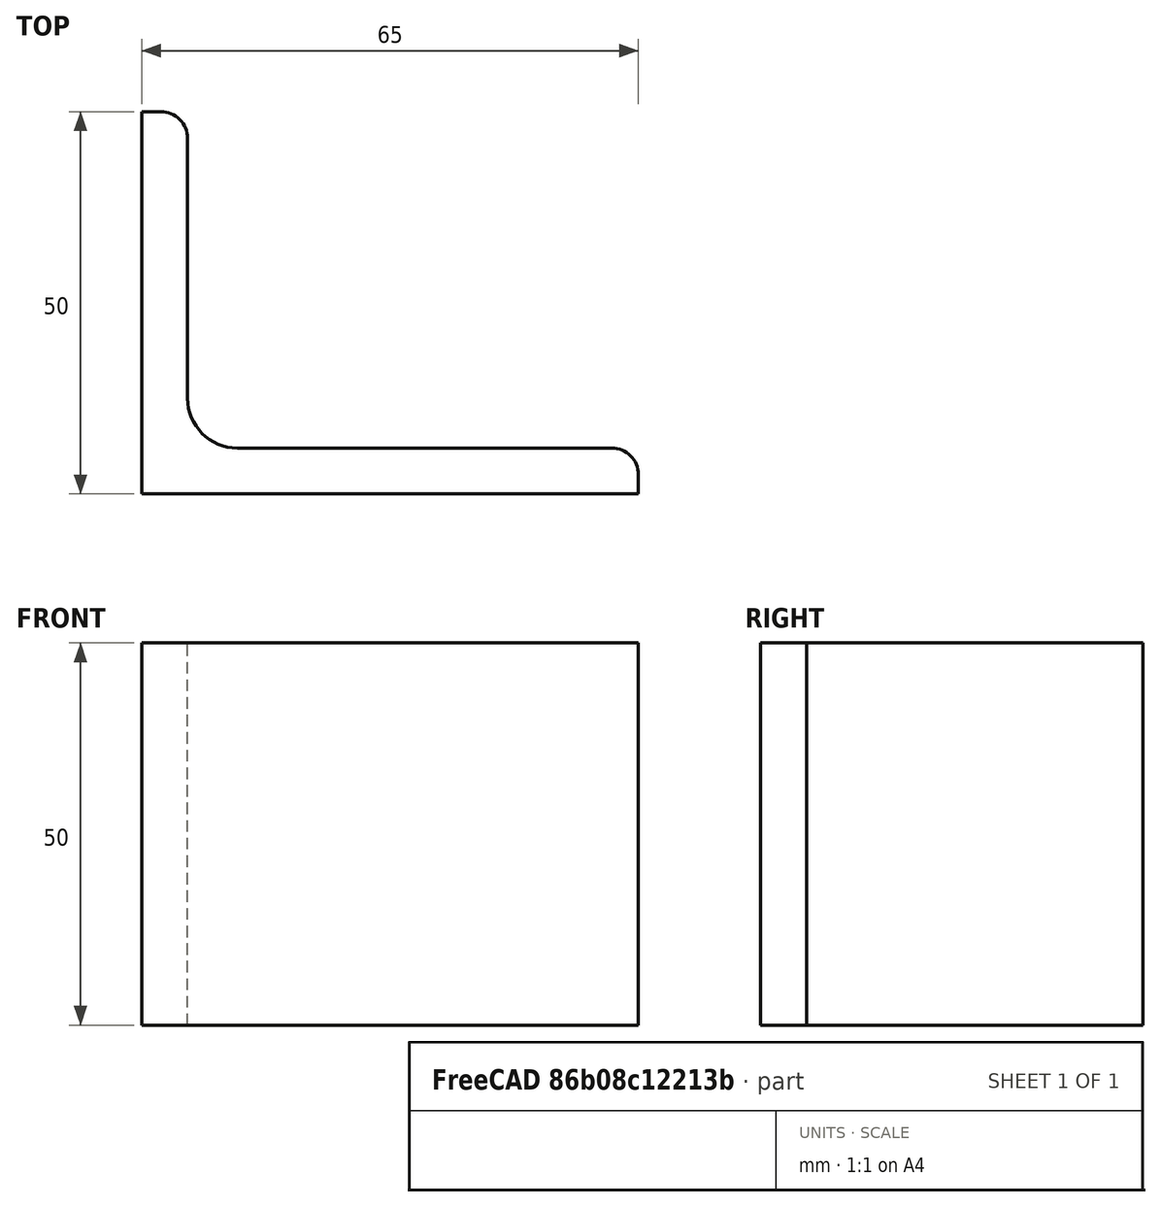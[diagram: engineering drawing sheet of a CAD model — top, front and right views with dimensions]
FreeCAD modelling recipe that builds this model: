
FCSTD DOCUMENT  (FreeCAD 0.15R4671 (Git))
Label: Angle Bar 65x50x6 EN10056 S235JR
License: All rights reserved
LicenseURL: http://en.wikipedia.org/wiki/All_rights_reserved
objects: Sketcher::SketchObject×1, Part::Extrusion×1
note: 2 computed .brp shape members not serialized (recipe doc carries the construction recipe); baked Part::Feature solids carry a one-line shape summary decoded from their .brp

FEATURE [Sketcher::SketchObject] Sketch
  sketch-geometry (9):
    g0: LineSegment StartX=0 StartY=0 StartZ=0 EndX=65 EndY=0 EndZ=0
    g1: LineSegment StartX=65 StartY=0 StartZ=0 EndX=65 EndY=2.5 EndZ=0
    g2: LineSegment StartX=61.5 StartY=6 StartZ=0 EndX=12.5 EndY=6 EndZ=0
    g3: LineSegment StartX=0 StartY=0 StartZ=0 EndX=0 EndY=50 EndZ=0
    g4: LineSegment StartX=0 StartY=50 StartZ=0 EndX=2.5 EndY=50 EndZ=0
    g5: LineSegment StartX=6 StartY=46.5 StartZ=0 EndX=6 EndY=12.5 EndZ=0
    g6: ArcOfCircle CenterX=12.5 CenterY=12.5 CenterZ=0 NormalX=0 NormalY=0 NormalZ=1 Radius=6.5 StartAngle=3.14159 EndAngle=4.71239
    g7: ArcOfCircle CenterX=2.5 CenterY=46.5 CenterZ=0 NormalX=0 NormalY=0 NormalZ=1 Radius=3.5 StartAngle=0 EndAngle=1.5708
    g8: ArcOfCircle CenterX=61.5 CenterY=2.5 CenterZ=0 NormalX=0 NormalY=0 NormalZ=1 Radius=3.5 StartAngle=0 EndAngle=1.5708
  constraints (23):
    c: Coincident(g0,g-1)
    c: Horizontal(g0)
    c: Coincident(g1,g0)
    c: Vertical(g1)
    c: Horizontal(g2)
    c: Coincident(g3,g-1)
    c: Vertical(g3)
    c: Coincident(g4,g3)
    c: Horizontal(g4)
    c: Vertical(g5)
    c: Tangent(g5,g6) = -1.5708
    c: Tangent(g2,g6) = 1.5708
    c: Tangent(g4,g7) = 1.5708
    c: Tangent(g5,g7) = 1.5708
    c: Tangent(g2,g8) = -1.5708
    c: Tangent(g1,g8) = -1.5708
    c: DistanceX(g0) = 65
    c: DistanceY(g3) = 50
    c: DistanceY(g0,g2) = 6
    c: DistanceX(g3,g5) = 6
    c: Radius(g6) = 6.5
    c: Radius(g8) = 3.5
    c: Radius(g7) = 3.5
FEATURE [Part::Extrusion] Extrude  label="Angle Bar 65x50x6 EN10056 S235JR"
  Base = -> Sketch
  Dir = (0,0,50)
  Solid = true
